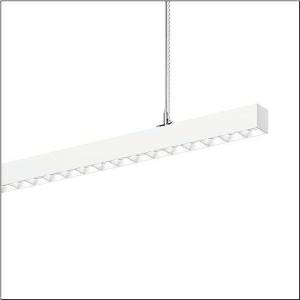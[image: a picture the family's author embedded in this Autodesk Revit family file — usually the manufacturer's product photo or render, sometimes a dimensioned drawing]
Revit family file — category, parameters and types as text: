
# Revit family: silica_21_51mx36dc3dwb
name_source: partatom
category: Lighting Fixtures
units: mm (PartAtom-declared; Revit-internal decimal feet)

## family parameters
Cut with Voids When Loaded = No
Host = Face
Light Source = No
Part Type = Normal
Room Calculation Point = No
Round Connector Dimension = Use Diameter
Shared = No

## types (1)
- --- (1 x LED, 17650 lm, 104.1 W, 3000K)
    Apparent Load = 104 VA
    CIE Flux Codes = 83 98 100 61 100
    Color Rendering = 80
    Color Temperature = 3000K
    Default Elevation = 1800 mm
    Description = Silica 21, office luminaire, primary light control with darklight reflector, of PMMA, white, CAT 2 (L<= 3000cd/m²), light emission: direct/indirect distribution, primary light characteristic: symmetric, installation type: suspended mounting, LED, rated luminous flux: 17.650lm, luminous efficacy: 170lm/W, light colour: 830, colour temperature: 3000K, control gear: DALI 2, with terminal, 3+2-pole, max. 2.5mm², mains connection: 220..240V, AC, 50/60Hz, rated input power: 104.1W, luminaire housing, of aluminium, traffic white (RAL 9016), length: 3.004mm, width: 53mm, height: 53mm, protection rating (complete): IP20, insulation class (complete): insulation class I (protective earthing), certification: CE, permissible operating ambient temperature: 0..+35°C, standard: EN 50419, packaging unit: 1 piece
    Height = 53 mm
    Lamp = 1 x LED
    Lamp Light Flux = 17650 lm
    Lamp Power = 104.1 W
    Lamp count = 1
    Length = 3004 mm
    Luminous efficacy = 170 lm/W
    Manufacturer = Siteco
    ModVariant = No
    Model = 51MX36DC3DWB
    Mounting Place = Ceiling
    Mounting Type = Pendant
    Number of Poles = 1
    OnlyDefault = Yes
    Power Factor = 1
    Product Name = Silica 21
    Product group = office luminaire | ceiling pendant
    ProductGroupID = 903
    Protection Class = Protection class I
    Protection Degree = IP 20
    RLX_Detail_Level = 1
    RLX_Emergency_Light_Flux = 0 lm
    RLX_Emergency_Type = 0
    RLX_Emergency_Type_DB = No
    RlxData = <blob elided: 62225 chars, md5=af7a9a46>
    Socket = socket
    Standby Power = 0 W
    System Light Flux = 17650 lm
    System Power = 104 W
    Type Comments = factory setting: luminous flux: 100 % | dim-lin: 254 | 359 mA
    Type Image = l_1335921.jpg
    URL = http://relux.com
    VarID = @adj_121605
    Voltage = 0 V
    Weight = 0.00 kg
    Width = 53 mm

## geometry (parser evidence)
native form markers: Blend x4, Sweep x12
no freeform markers — native parametric forms only
